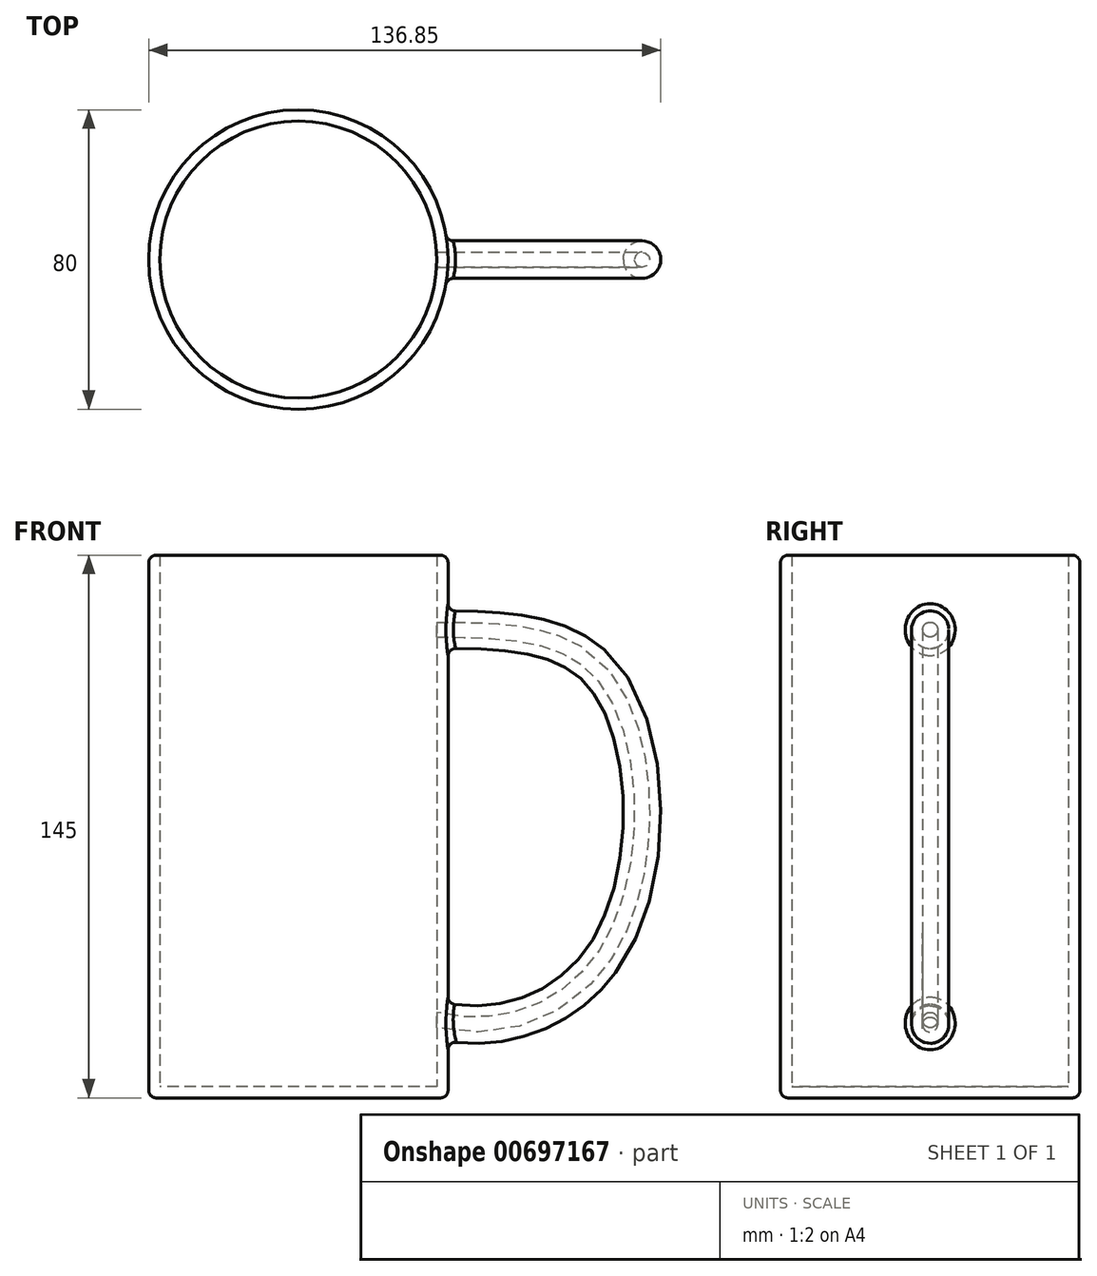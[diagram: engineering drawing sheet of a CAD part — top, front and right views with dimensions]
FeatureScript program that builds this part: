
annotation { "Feature Type Name" : "Feature", "Feature Type Description" : "" }
export const myFeature = defineFeature(function(context is Context, id is Id, definition is map)
    precondition{}
    {
        {
            var Q0;
            Q0=qCreatedBy(makeId("Top.planeOp"),FACE);
            var sketch = newSketch(context, id + "F0", { "sketchPlane" : qUnion([Q0])});
            skCircle(sketch, "E0", {"center": v(0, 0) * mm, "radius": 40 * mm});
            skSolve(sketch);
        }
        {
            var Q0;
            Q0 = qSketchRegion(id + "F0", true);
            extrude(context, id + "F1", {"entities" : qUnion([Q0]), "depth" : 145 * mm, "offsetDistance" : 25 * mm});
        }
        {
            var Q0;
            Q0=qCreatedBy(makeId("Front.planeOp"),FACE);
            var sketch = newSketch(context, id + "F2", { "sketchPlane" : qUnion([Q0])});
            skFitSpline(sketch, "E1", {"points": [v(35.7, 125.83) * mm, v(82, 113.4) * mm, v(83.95, 40.1) * mm, v(35.42, 20.53) * mm], "startDerivative": vector(169.32, -1.94) * mm, "endDerivative": vector(-172.23, 47.68) * mm});
            skSolve(sketch);
        }
        {
            var Q0;
            Q0=qCreatedBy(makeId("Right.planeOp"),FACE);
            cPlane(context, id + "F3", {"entities" : qUnion([Q0]), "cplaneType" : CPlaneType.OFFSET, "offset" : 35.3 * mm, "width" : 150 * mm, "height" : 150 * mm});
        }
        {
            var Q0;
            Q0=qCreatedBy(id+"F3.planeOp",FACE);
            var sketch = newSketch(context, id + "F4", { "sketchPlane" : qUnion([Q0])});
            skCircle(sketch, "E2", {"center": v(0, 125.16) * mm, "radius": 5 * mm});
            skSolve(sketch);
        }
        {
            var Q0;
            Q0 = qSketchRegion(id + "F4", true);
            var Q1;
            Q1=sQuery(id+"F2.wireOp",EDGE,"E1");
            sweep(context, id + "F5", {"operationType" : NewBodyOperationType.ADD, "profiles" : qUnion([Q0]), "path" : qUnion([Q1])});
        }
        {
            var Q0;
            Q0=makeQuery(id+"F1.opExtrude","CAP_FACE",FACE,{"disambiguationData":[OSD([sQuery(id+"F0.wireOp",EDGE,"E0")])],"isStart":false});
            shell(context, id + "F6", {"entities" : qUnion([Q0]), "thickness" : 3 * mm});
        }
        {
            var Q0;
            Q0=makeQuery(id+"F1.opExtrude","CAP_EDGE",EDGE,{"disambiguationData":[OSD([sQuery(id+"F0.wireOp",EDGE,"E0")])],"isStart":false});
            var Q1;
            Q1=makeQuery(id+"F1.opExtrude","CAP_EDGE",EDGE,{"disambiguationData":[OSD([sQuery(id+"F0.wireOp",EDGE,"E0")])],"isStart":true});
            var Q2;
            Q2=makeQuery(id+"F5.boolean.opBoolean","INTERSECT",EDGE,{"disambiguationData":[OD(1.0)],"derivedFrom":[makeQuery(id+"F1.opExtrude","SWEPT_FACE",FACE,{"disambiguationData":[OSD([sQuery(id+"F0.wireOp",EDGE,"E0")])]}),makeQuery(id+"F5.opSweep","SWEPT_FACE",FACE,{"disambiguationData":[OSD([sQuery(id+"F2.wireOp",EDGE,"E1"),sQuery(id+"F4.wireOp",EDGE,"E2")])]})]});
            var Q3;
            Q3=makeQuery(id+"F5.boolean.opBoolean","INTERSECT",EDGE,{"disambiguationData":[OD(0.0)],"derivedFrom":[makeQuery(id+"F1.opExtrude","SWEPT_FACE",FACE,{"disambiguationData":[OSD([sQuery(id+"F0.wireOp",EDGE,"E0")])]}),makeQuery(id+"F5.opSweep","SWEPT_FACE",FACE,{"disambiguationData":[OSD([sQuery(id+"F2.wireOp",EDGE,"E1"),sQuery(id+"F4.wireOp",EDGE,"E2")])]})]});
            fillet(context, id + "F7", {"entities" : qUnion([Q0, Q1, Q2, Q3]), "radius" : 2 * mm, "tangentPropagation" : true, "allowEdgeOverflow" : false});
        }
    });
